# Revit family: O61061001 ORINAL ARRECIFE
name_source: partatom
category: Aparatos sanitarios
revit_build: Autodesk Revit 2016 (Build: 20151007_0715(x64)
units: mm (PartAtom-declared; Revit-internal decimal feet)

## family parameters
Anfitrión = Muro
Compartido = No
Corte con vacíos al cargar = No
Cota de conector redondo = Diámetro de uso
Número OmniClass = 23.45.05.00
Punto de cálculo de habitación = No
Siempre vertical = Sí
Tipo de pieza = Normal
Título OmniClass = Sanitary Equipment

## types (1)
- Tipo 1
    Acabado = Brillante
    Alto Nominal = 572 mm
    Ancho Nominal = 300 mm  [stored 0.984252 ft]
    Característica = Diseño moderno de formas orgánicas de tráfico medio, sifón integrado en porcelana.
    Color = Blanco
    Consumo de Agua = 1.9 lpf o 0,5 gpf.
    Cumplimiento de Norma = ASME A112.19.2-2008 / CSA B45.1 - 08 y NTC 920(ICONTEC).
    Código de montaje = D2010210
    Descripción de la garantía = Garantia Corona Limintada de por vida para la porcelana
    Diámetro de conexión de entrada = 1.9 cm / 3/4"
    Diámetro de conexión sanitaria = 2.54 cm ( 1" )
    Duración Garantía Unidad = Años
    Fabricante = www.corona.com.co
    Forma = Ovalado
    Imagen de tipo = <Ninguno>
    Informacion del producto = https://www.corona.co
    Longitud Nominal = 352 mm  [stored 1.15486 ft]
    Material = Ceramica_Corona_Blanco
    Material Secundario = Plastico_Corona_Blanco
    Material de Fabricación = Porcelana Sanitaria Vitrificada
    Modelo = 061061001
    Nombre = Orinal de entrada superior Arrecife
    Numero de Modelo = 061061001
    Presión máxima = 80 PSI.
    Presión mínima = 25 PSI.
    Responsable Garantia Partes = www.corona.com.co
    Tamaño = 352 x 572 x 300 mm
    Tipo de Activo = Fijo
    URL = https://www.corona.co

note: [stored X ft] marks values corroborated as IEEE doubles in the binary element streams (Revit-internal decimal feet)
